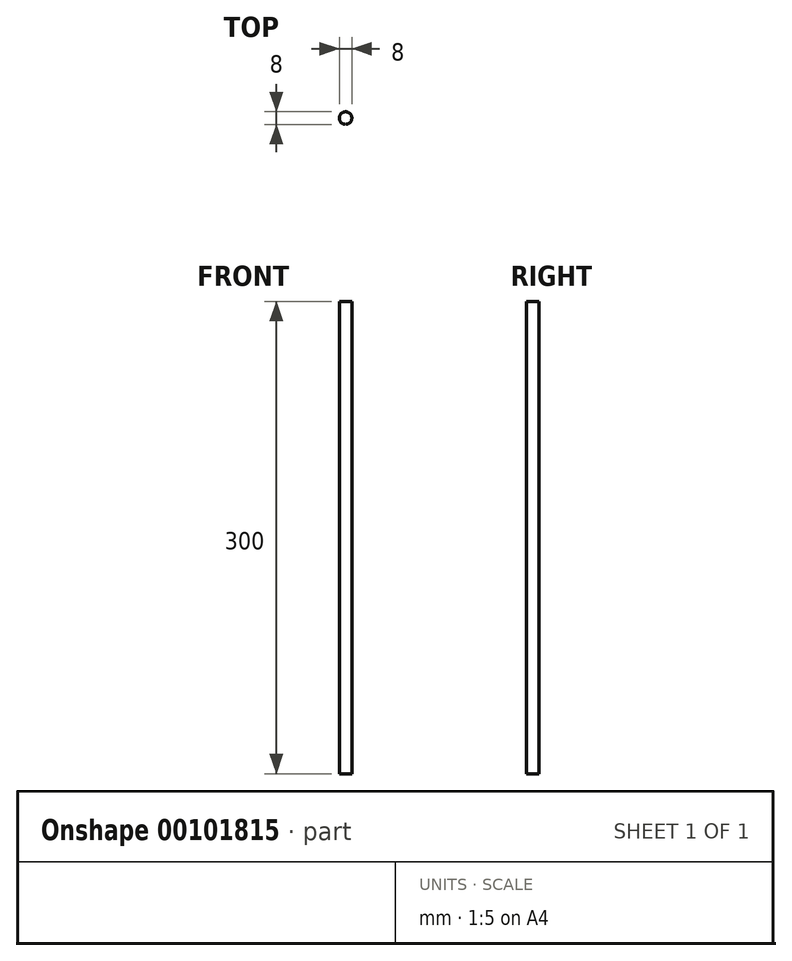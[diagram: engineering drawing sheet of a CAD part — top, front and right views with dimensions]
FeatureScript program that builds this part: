
annotation { "Feature Type Name" : "Feature", "Feature Type Description" : "" }
export const myFeature = defineFeature(function(context is Context, id is Id, definition is map)
    precondition{}
    {
        {
            var Q0;
            Q0=qCreatedBy(makeId("Top.planeOp"),FACE);
            var sketch = newSketch(context, id + "F0", { "sketchPlane" : qUnion([Q0])});
            skCircle(sketch, "E0", {"center": v(0, 0) * mm, "radius": 4 * mm});
            skSolve(sketch);
        }
        {
            var Q0;
            Q0=makeQuery(id+"F0.imprint","IMPRINT",FACE,{"disambiguationData":[TD([[makeQuery(id+"F0.imprint","IMPRINT",EDGE,{"derivedFrom":sQuery(id+"F0.wireOp",EDGE,"E0")}),1.0]])]});
            extrude(context, id + "F1", {"entities" : qUnion([Q0]), "depth" : 300 * mm});
        }
    });
